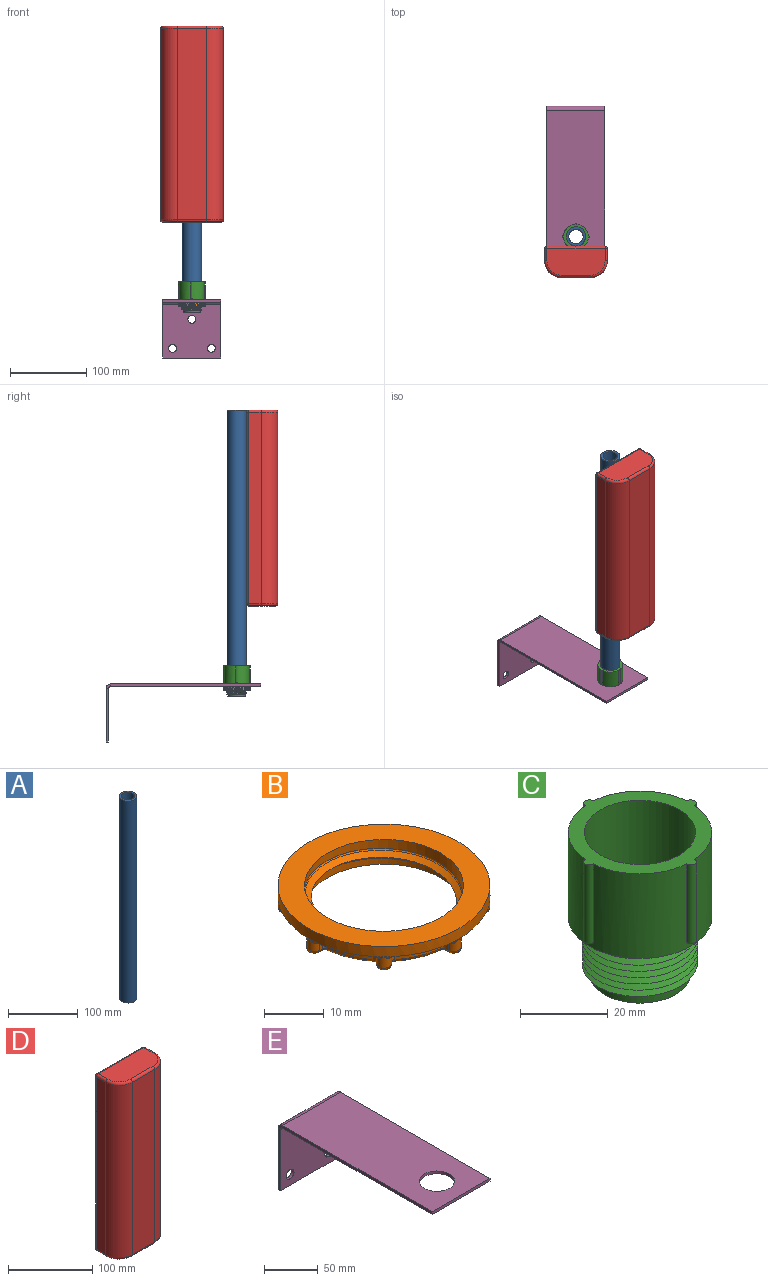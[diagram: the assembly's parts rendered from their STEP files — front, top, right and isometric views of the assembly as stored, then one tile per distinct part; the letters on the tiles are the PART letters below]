
ASSEMBLY  parts=5 mates=4
PART A: 4 faces, bbox 25.4x25.4x355.6 mm
  f0: cylinder r=9.53mm len=355.6mm, axis (0,0,-1), area 21281.7mm2, adj f2,f3
  f1: cylinder r=12.7mm len=355.6mm, axis (0,0,-1), area 28375.6mm2, adj f2,f3
  f2: plane 25.4x25.4mm, normal (0,0,1), area 221.7mm2, adj f0,f1
  f3: plane 25.4x25.4mm, normal (0,0,-1), area 221.7mm2, adj f0,f1
PART B: 196 faces, bbox 36.3x36.3x5.1 mm
  f0: cylinder r=13.33mm len=26.67mm, axis (0,0,1), area 256.3mm2, adj f17,f19,f184,f185,f188,f189,f192,f193
  f1: cylinder r=15.39mm len=7.68mm, axis (0,0,1), area 14.3mm2, adj f20,f57,f75,f157
  f2: plane 10.02x5.12mm, normal (0,0,-1), area 16.9mm2, adj f15,f136,f137,f139,f141,f142
  f3: cylinder r=15.39mm len=7.68mm, axis (0,0,1), area 14.3mm2, adj f52,f55,f87,f139
  f4: plane 10.02x5.12mm, normal (0,0,-1), area 16.9mm2, adj f15,f118,f119,f121,f123,f124
  f5: cylinder r=15.39mm len=7.68mm, axis (0,0,1), area 14.3mm2, adj f47,f50,f99,f121
  f6: plane 10.02x5.12mm, normal (0,0,-1), area 16.9mm2, adj f15,f62,f63,f64,f65,f68
  f7: cylinder r=15.39mm len=7.68mm, axis (0,0,1), area 14.3mm2, adj f42,f45,f68,f111
  f8: plane 10.02x5.12mm, normal (0,0,-1), area 16.9mm2, adj f15,f127,f128,f130,f132,f134
  f9: cylinder r=15.39mm len=7.68mm, axis (0,0,1), area 14.3mm2, adj f37,f40,f110,f130
  f10: plane 10.02x5.12mm, normal (0,0,-1), area 16.9mm2, adj f15,f145,f146,f148,f150,f152
  f11: cylinder r=15.39mm len=7.68mm, axis (0,0,1), area 14.3mm2, adj f32,f35,f98,f148
  f12: plane 10.02x5.12mm, normal (0,0,-1), area 16.9mm2, adj f15,f163,f164,f166,f168,f170
  f13: plane 10.02x5.12mm, normal (0,0,-1), area 16.9mm2, adj f15,f172,f173,f175,f177,f178
  f14: cylinder r=15.39mm len=7.68mm, axis (0,0,1), area 14.3mm2, adj f27,f30,f86,f166
  f15: cylinder r=17.78mm len=35.56mm, axis (0,0,1), area 235.5mm2, adj f2,f4,f6,f8,f10,f12,f13,f16
  f16: plane 10.02x5.12mm, normal (0,0,-1), area 16.9mm2, adj f15,f154,f155,f157,f159,f160
  f17: plane 35.56x35.56mm, normal (0,0,1), area 434.5mm2, adj f0,f15
  f18: cylinder r=15.39mm len=7.68mm, axis (0,0,1), area 14.3mm2, adj f22,f25,f74,f175
  f19: plane 34.29x34.29mm, normal (0,0,-1), area 152.9mm2, adj f0,f69,f70,f71,f72,f73,f74,f75
  f20: cylinder r=0.64mm len=1.7mm, axis (0,0,-1), area 1.6mm2, adj f1,f21,f73,f156
  f21: plane 1.7x0.6mm, normal (-1,0,0), area 1mm2, adj f20,f23,f71,f155
  f22: cylinder r=0.64mm len=1.7mm, axis (0,0,-1), area 1.6mm2, adj f18,f24,f72,f176
  f23: cylinder r=1.27mm len=2.54mm, axis (0,0,-1), area 7.5mm2, adj f21,f24,f69,f153,f154,f178,f179
  f24: plane 1.7x0.6mm, normal (1,0,0), area 1mm2, adj f22,f23,f70,f177
  f25: cylinder r=0.64mm len=1.7mm, axis (0,0,-1), area 1.6mm2, adj f18,f26,f76,f174
  f26: plane 1.7x0.42mm, normal (-0.71,0.71,0), area 1mm2, adj f25,f28,f78,f173
  f27: cylinder r=0.64mm len=1.7mm, axis (0,0,-1), area 1.6mm2, adj f14,f29,f84,f165
  f28: cylinder r=1.27mm len=2.34mm, axis (0,0,-1), area 7.5mm2, adj f26,f29,f80,f162,f163,f171,f172
  f29: plane 1.7x0.42mm, normal (0.71,-0.71,0), area 1mm2, adj f27,f28,f82,f164
  f30: cylinder r=0.64mm len=1.7mm, axis (0,0,-1), area 1.6mm2, adj f14,f31,f88,f167
  f31: plane 1.7x0.6mm, normal (0,1,0), area 1mm2, adj f30,f33,f90,f168
  f32: cylinder r=0.64mm len=1.7mm, axis (0,0,-1), area 1.6mm2, adj f11,f34,f96,f147
  f33: cylinder r=1.27mm len=2.54mm, axis (0,0,-1), area 7.5mm2, adj f31,f34,f92,f144,f145,f169,f170
  f34: plane 1.7x0.6mm, normal (0,-1,0), area 1mm2, adj f32,f33,f94,f146
  f35: cylinder r=0.64mm len=1.7mm, axis (0,0,-1), area 1.6mm2, adj f11,f36,f100,f149
  f36: plane 1.7x0.42mm, normal (0.71,0.71,0), area 1mm2, adj f35,f38,f102,f150
  f37: cylinder r=0.64mm len=1.7mm, axis (0,0,-1), area 1.6mm2, adj f9,f39,f108,f129
  f38: cylinder r=1.27mm len=2.34mm, axis (0,0,-1), area 7.5mm2, adj f36,f39,f104,f126,f127,f151,f152
  f39: plane 1.7x0.42mm, normal (-0.71,-0.71,0), area 1mm2, adj f37,f38,f106,f128
  f40: cylinder r=0.64mm len=1.7mm, axis (0,0,-1), area 1.6mm2, adj f9,f41,f112,f131
  f41: plane 1.7x0.6mm, normal (1,0,0), area 1mm2, adj f40,f43,f114,f132
  f42: cylinder r=0.64mm len=1.7mm, axis (0,0,-1), area 1.6mm2, adj f7,f44,f66,f113
  f43: cylinder r=1.27mm len=2.54mm, axis (0,0,-1), area 7.5mm2, adj f41,f44,f60,f62,f116,f133,f134
  f44: plane 1.7x0.6mm, normal (-1,0,0), area 1mm2, adj f42,f43,f64,f115
  f45: cylinder r=0.64mm len=1.7mm, axis (0,0,-1), area 1.6mm2, adj f7,f46,f67,f109
  f46: plane 1.7x0.42mm, normal (0.71,-0.71,0), area 1mm2, adj f45,f48,f65,f107
  f47: cylinder r=0.64mm len=1.7mm, axis (0,0,-1), area 1.6mm2, adj f5,f49,f101,f122
  f48: cylinder r=1.27mm len=2.34mm, axis (0,0,-1), area 7.5mm2, adj f46,f49,f61,f63,f105,f124,f125
  f49: plane 1.7x0.42mm, normal (-0.71,0.71,0), area 1mm2, adj f47,f48,f103,f123
  f50: cylinder r=0.64mm len=1.7mm, axis (0,0,-1), area 1.6mm2, adj f5,f51,f97,f120
  f51: plane 1.7x0.6mm, normal (0,-1,0), area 1mm2, adj f50,f53,f95,f119
  f52: cylinder r=0.64mm len=1.7mm, axis (0,0,-1), area 1.6mm2, adj f3,f54,f89,f140
  f53: cylinder r=1.27mm len=2.54mm, axis (0,0,-1), area 7.5mm2, adj f51,f54,f93,f117,f118,f142,f143
  f54: plane 1.7x0.6mm, normal (0,1,0), area 1mm2, adj f52,f53,f91,f141
  f55: cylinder r=0.64mm len=1.7mm, axis (0,0,-1), area 1.6mm2, adj f3,f56,f85,f138
  f56: plane 1.7x0.42mm, normal (-0.71,-0.71,0), area 1mm2, adj f55,f58,f83,f137
  f57: cylinder r=0.64mm len=1.7mm, axis (0,0,-1), area 1.6mm2, adj f1,f59,f77,f158
  f58: cylinder r=1.27mm len=2.34mm, axis (0,0,-1), area 7.5mm2, adj f56,f59,f81,f135,f136,f160,f161
  f59: plane 1.7x0.42mm, normal (0.71,0.71,0), area 1mm2, adj f57,f58,f79,f159
  f60: bspline ~1.51x0.66mm, area 0.4mm2, adj f15,f43,f62
  f61: bspline ~1.12x1.02mm, area 0.4mm2, adj f15,f48,f63
  f62: torus R=1.91mm, axis (0,0,1), area 1mm2, adj f6,f43,f60,f64
  f63: torus R=1.91mm, axis (0,0,1), area 1mm2, adj f6,f48,f61,f65
  f64: cylinder r=0.64mm len=0.64mm, axis (0,1,0), area 0.6mm2, adj f6,f44,f62,f66
  f65: cylinder r=0.64mm len=0.87mm, axis (-0.71,-0.71,0), area 0.6mm2, adj f6,f46,f63,f67
  f66: sphere r=0.64mm, area 0.4mm2, adj f42,f64,f68
  f67: sphere r=0.64mm, area 0.7mm2, adj f45,f65,f68
  f68: torus R=16.03mm, axis (0,0,1), area 8.5mm2, adj f6,f7,f66,f67
  f69: torus R=0.64mm, axis (0,0,-1), area 3.3mm2, adj f19,f23,f70,f71
  f70: cylinder r=0.64mm len=0.64mm, axis (0,-1,0), area 0.6mm2, adj f19,f24,f69,f72
  f71: cylinder r=0.64mm len=0.64mm, axis (0,1,0), area 0.6mm2, adj f19,f21,f69,f73
  f72: torus R=1.27mm, axis (0,0,-1), area 1.3mm2, adj f19,f22,f70,f74
  f73: torus R=1.27mm, axis (0,0,-1), area 1.3mm2, adj f19,f20,f71,f75
  f74: torus R=14.76mm, axis (0,0,-1), area 8.3mm2, adj f18,f19,f72,f76
  f75: torus R=14.76mm, axis (0,0,-1), area 8.3mm2, adj f1,f19,f73,f77
  f76: torus R=1.27mm, axis (0,0,-1), area 1.3mm2, adj f19,f25,f74,f78
  f77: torus R=1.27mm, axis (0,0,-1), area 1.3mm2, adj f19,f57,f75,f79
  f78: cylinder r=0.64mm len=0.87mm, axis (0.71,0.71,0), area 0.6mm2, adj f19,f26,f76,f80
  f79: cylinder r=0.64mm len=0.87mm, axis (0.71,-0.71,0), area 0.6mm2, adj f19,f59,f77,f81
  f80: torus R=0.64mm, axis (0,0,-1), area 3.3mm2, adj f19,f28,f78,f82
  f81: torus R=0.64mm, axis (0,0,-1), area 3.3mm2, adj f19,f58,f79,f83
  f82: cylinder r=0.64mm len=0.87mm, axis (-0.71,-0.71,0), area 0.6mm2, adj f19,f29,f80,f84
  f83: cylinder r=0.64mm len=0.87mm, axis (-0.71,0.71,0), area 0.6mm2, adj f19,f56,f81,f85
  f84: torus R=1.27mm, axis (0,0,-1), area 1.3mm2, adj f19,f27,f82,f86
  f85: torus R=1.27mm, axis (0,0,-1), area 1.3mm2, adj f19,f55,f83,f87
  f86: torus R=14.76mm, axis (0,0,-1), area 8.3mm2, adj f14,f19,f84,f88
  f87: torus R=14.76mm, axis (0,0,-1), area 8.3mm2, adj f3,f19,f85,f89
  f88: torus R=1.27mm, axis (0,0,-1), area 1.3mm2, adj f19,f30,f86,f90
  f89: torus R=1.27mm, axis (0,0,-1), area 1.3mm2, adj f19,f52,f87,f91
  f90: cylinder r=0.64mm len=0.64mm, axis (1,0,0), area 0.6mm2, adj f19,f31,f88,f92
  f91: cylinder r=0.64mm len=0.64mm, axis (1,0,0), area 0.6mm2, adj f19,f54,f89,f93
  f92: torus R=0.64mm, axis (0,0,-1), area 3.3mm2, adj f19,f33,f90,f94
  f93: torus R=0.64mm, axis (0,0,-1), area 3.3mm2, adj f19,f53,f91,f95
  f94: cylinder r=0.64mm len=0.64mm, axis (-1,0,0), area 0.6mm2, adj f19,f34,f92,f96
  f95: cylinder r=0.64mm len=0.64mm, axis (-1,0,0), area 0.6mm2, adj f19,f51,f93,f97
  f96: torus R=1.27mm, axis (0,0,-1), area 1.3mm2, adj f19,f32,f94,f98
  f97: torus R=1.27mm, axis (0,0,-1), area 1.3mm2, adj f19,f50,f95,f99
  f98: torus R=14.76mm, axis (0,0,-1), area 8.3mm2, adj f11,f19,f96,f100
  f99: torus R=14.76mm, axis (0,0,-1), area 8.3mm2, adj f5,f19,f97,f101
  f100: torus R=1.27mm, axis (0,0,-1), area 1.3mm2, adj f19,f35,f98,f102
  f101: torus R=1.27mm, axis (0,0,-1), area 1.3mm2, adj f19,f47,f99,f103
  f102: cylinder r=0.64mm len=0.87mm, axis (0.71,-0.71,0), area 0.6mm2, adj f19,f36,f100,f104
  f103: cylinder r=0.64mm len=0.87mm, axis (0.71,0.71,0), area 0.6mm2, adj f19,f49,f101,f105
  f104: torus R=0.64mm, axis (0,0,-1), area 3.3mm2, adj f19,f38,f102,f106
  f105: torus R=0.64mm, axis (0,0,-1), area 3.3mm2, adj f19,f48,f103,f107
  f106: cylinder r=0.64mm len=0.87mm, axis (-0.71,0.71,0), area 0.6mm2, adj f19,f39,f104,f108
  f107: cylinder r=0.64mm len=0.87mm, axis (-0.71,-0.71,0), area 0.6mm2, adj f19,f46,f105,f109
  f108: torus R=1.27mm, axis (0,0,-1), area 1.3mm2, adj f19,f37,f106,f110
  f109: torus R=1.27mm, axis (0,0,-1), area 1.3mm2, adj f19,f45,f107,f111
  f110: torus R=14.76mm, axis (0,0,-1), area 8.3mm2, adj f9,f19,f108,f112
  f111: torus R=14.76mm, axis (0,0,-1), area 8.3mm2, adj f7,f19,f109,f113
  f112: torus R=1.27mm, axis (0,0,-1), area 1.3mm2, adj f19,f40,f110,f114
  f113: torus R=1.27mm, axis (0,0,-1), area 1.3mm2, adj f19,f42,f111,f115
  f114: cylinder r=0.64mm len=0.64mm, axis (0,-1,0), area 0.6mm2, adj f19,f41,f112,f116
  f115: cylinder r=0.64mm len=0.64mm, axis (0,1,0), area 0.6mm2, adj f19,f44,f113,f116
  f116: torus R=0.64mm, axis (0,0,-1), area 3.3mm2, adj f19,f43,f114,f115
  f117: bspline ~1.51x0.66mm, area 0.6mm2, adj f15,f53,f118
  f118: torus R=1.91mm, axis (0,0,1), area 1mm2, adj f4,f53,f117,f119
  f119: cylinder r=0.64mm len=0.64mm, axis (-1,0,0), area 0.6mm2, adj f4,f51,f118,f120
  f120: sphere r=0.64mm, area 0.4mm2, adj f50,f119,f121
  f121: torus R=16.03mm, axis (0,0,1), area 8.5mm2, adj f4,f5,f120,f122
  f122: sphere r=0.64mm, area 0.6mm2, adj f47,f121,f123
  f123: cylinder r=0.64mm len=0.87mm, axis (0.71,0.71,0), area 0.6mm2, adj f4,f49,f122,f124
  f124: torus R=1.91mm, axis (0,0,1), area 1mm2, adj f4,f48,f123,f125
  f125: bspline ~1.12x1.02mm, area 0.4mm2, adj f15,f48,f124
  f126: bspline ~1.12x1.02mm, area 0.4mm2, adj f15,f38,f127
  f127: torus R=1.91mm, axis (0,0,1), area 1mm2, adj f8,f38,f126,f128
  f128: cylinder r=0.64mm len=0.87mm, axis (-0.71,0.71,0), area 0.6mm2, adj f8,f39,f127,f129
  f129: sphere r=0.64mm, area 0.7mm2, adj f37,f128,f130
  f130: torus R=16.03mm, axis (0,0,1), area 8.5mm2, adj f8,f9,f129,f131
  f131: sphere r=0.64mm, area 0.8mm2, adj f40,f130,f132
  f132: cylinder r=0.64mm len=0.64mm, axis (0,-1,0), area 0.6mm2, adj f8,f41,f131,f134
  f133: bspline ~1.51x0.66mm, area 0.4mm2, adj f15,f43,f134
  f134: torus R=1.91mm, axis (0,0,1), area 1mm2, adj f8,f43,f132,f133
  f135: bspline ~1.12x1.02mm, area 0.4mm2, adj f15,f58,f136
  f136: torus R=1.91mm, axis (0,0,1), area 1mm2, adj f2,f58,f135,f137
  f137: cylinder r=0.64mm len=0.87mm, axis (-0.71,0.71,0), area 0.6mm2, adj f2,f56,f136,f138
  f138: sphere r=0.64mm, area 0.6mm2, adj f55,f137,f139
  f139: torus R=16.03mm, axis (0,0,1), area 8.5mm2, adj f2,f3,f138,f140
  f140: sphere r=0.64mm, area 0.6mm2, adj f52,f139,f141
  f141: cylinder r=0.64mm len=0.64mm, axis (1,0,0), area 0.6mm2, adj f2,f54,f140,f142
  f142: torus R=1.91mm, axis (0,0,1), area 1mm2, adj f2,f53,f141,f143
  f143: bspline ~1.51x0.66mm, area 0.4mm2, adj f15,f53,f142
  f144: bspline ~1.51x0.66mm, area 0.4mm2, adj f15,f33,f145
  f145: torus R=1.91mm, axis (0,0,1), area 1mm2, adj f10,f33,f144,f146
  f146: cylinder r=0.64mm len=0.64mm, axis (-1,0,0), area 0.6mm2, adj f10,f34,f145,f147
  f147: sphere r=0.64mm, area 0.6mm2, adj f32,f146,f148
  f148: torus R=16.03mm, axis (0,0,1), area 8.5mm2, adj f10,f11,f147,f149
  f149: sphere r=0.64mm, area 0.7mm2, adj f35,f148,f150
  f150: cylinder r=0.64mm len=0.87mm, axis (0.71,-0.71,0), area 0.6mm2, adj f10,f36,f149,f152
  f151: bspline ~1.12x1.02mm, area 0.4mm2, adj f15,f38,f152
  f152: torus R=1.91mm, axis (0,0,1), area 1mm2, adj f10,f38,f150,f151
  f153: bspline ~1.51x0.66mm, area 0.6mm2, adj f15,f23,f154
  f154: torus R=1.91mm, axis (0,0,1), area 1mm2, adj f16,f23,f153,f155
  f155: cylinder r=0.64mm len=0.64mm, axis (0,1,0), area 0.6mm2, adj f16,f21,f154,f156
  f156: sphere r=0.64mm, area 0.6mm2, adj f20,f155,f157
  f157: torus R=16.03mm, axis (0,0,1), area 8.5mm2, adj f1,f16,f156,f158
  f158: sphere r=0.64mm, area 0.6mm2, adj f57,f157,f159
  f159: cylinder r=0.64mm len=0.87mm, axis (0.71,-0.71,0), area 0.6mm2, adj f16,f59,f158,f160
  f160: torus R=1.91mm, axis (0,0,1), area 1mm2, adj f16,f58,f159,f161
  f161: bspline ~1.12x1.02mm, area 0.4mm2, adj f15,f58,f160
  f162: bspline ~1.12x1.02mm, area 0.4mm2, adj f15,f28,f163
  f163: torus R=1.91mm, axis (0,0,1), area 1mm2, adj f12,f28,f162,f164
  f164: cylinder r=0.64mm len=0.87mm, axis (-0.71,-0.71,0), area 0.6mm2, adj f12,f29,f163,f165
  f165: sphere r=0.64mm, area 0.8mm2, adj f27,f164,f166
  f166: torus R=16.03mm, axis (0,0,1), area 8.5mm2, adj f12,f14,f165,f167
  f167: sphere r=0.64mm, area 0.8mm2, adj f30,f166,f168
  f168: cylinder r=0.64mm len=0.64mm, axis (1,0,0), area 0.6mm2, adj f12,f31,f167,f170
  f169: bspline ~1.51x0.66mm, area 0.6mm2, adj f15,f33,f170
  f170: torus R=1.91mm, axis (0,0,1), area 1mm2, adj f12,f33,f168,f169
  f171: bspline ~1.12x1.02mm, area 0.4mm2, adj f15,f28,f172
  f172: torus R=1.91mm, axis (0,0,1), area 1mm2, adj f13,f28,f171,f173
  f173: cylinder r=0.64mm len=0.87mm, axis (0.71,0.71,0), area 0.6mm2, adj f13,f26,f172,f174
  f174: sphere r=0.64mm, area 0.6mm2, adj f25,f173,f175
  f175: torus R=16.03mm, axis (0,0,1), area 8.5mm2, adj f13,f18,f174,f176
  f176: sphere r=0.64mm, area 0.6mm2, adj f22,f175,f177
  f177: cylinder r=0.64mm len=0.64mm, axis (0,-1,0), area 0.6mm2, adj f13,f24,f176,f178
  f178: torus R=1.91mm, axis (0,0,1), area 1mm2, adj f13,f23,f177,f179
  f179: bspline ~1.51x0.66mm, area 0.5mm2, adj f15,f23,f178
  f180: bspline ~30.8x26.67mm, area 94mm2, adj f181,f184,f186,f187,f191
  f181: bspline ~30.8x26.67mm, area 93.9mm2, adj f180,f186,f190,f191,f195
  f182: plane 0.29x0.2mm, normal (-1,0,0), area 0mm2, adj f186,f189,f190
  f183: plane 0.29x0.2mm, normal (1,0,0), area 0mm2, adj f187,f191,f192
  f184: bspline ~26.68x26.62mm, area 28.6mm2, adj f0,f180,f185,f188
  f185: bspline ~1.15x0.87mm, area 0.4mm2, adj f0,f184,f186,f189
  f186: bspline ~1.64x1.35mm, area 0.5mm2, adj f180,f181,f182,f185,f190
  f187: bspline ~1.57x1.28mm, area 0.4mm2, adj f180,f183,f188,f191
  f188: bspline ~0.99x0.85mm, area 0.4mm2, adj f0,f184,f187,f192
  f189: cylinder r=0.38mm len=0.38mm, axis (0,0,1), area 0.2mm2, adj f0,f182,f185,f193
  f190: bspline ~1.57x1.29mm, area 0.4mm2, adj f181,f182,f186,f193
  f191: bspline ~1.65x1.35mm, area 0.5mm2, adj f180,f181,f183,f187,f194
  f192: cylinder r=0.38mm len=0.38mm, axis (0,0,1), area 0.2mm2, adj f0,f183,f188,f194
  f193: bspline ~0.99x0.85mm, area 0.4mm2, adj f0,f189,f190,f195
  f194: bspline ~1.15x0.87mm, area 0.4mm2, adj f0,f191,f192,f195
  f195: bspline ~26.68x26.62mm, area 28.6mm2, adj f0,f181,f193,f194
PART C: 29 faces, bbox 36.5x36.5x40.7 mm
  f0: cylinder r=11.56mm len=23.11mm, axis (0,0,1), area 129.3mm2, adj f1,f23,f24,f25,f27
  f1: cylinder r=11.56mm len=23.11mm, axis (0,0,1), area 4.3mm2, adj f0,f2,f27,f28
  f2: cylinder r=11.56mm len=23.11mm, axis (0,0,1), area 4.2mm2, adj f1,f3,f27,f28
  f3: cylinder r=11.56mm len=23.11mm, axis (0,0,1), area 4.3mm2, adj f2,f4,f27,f28
  f4: cylinder r=11.56mm len=23.11mm, axis (0,0,1), area 4.3mm2, adj f3,f5,f27,f28
  f5: cylinder r=11.56mm len=23.11mm, axis (0,0,1), area 4.3mm2, adj f4,f6,f27,f28
  f6: cylinder r=11.56mm len=23.11mm, axis (0,0,1), area 4.3mm2, adj f5,f7,f27,f28
  f7: cylinder r=11.56mm len=23.11mm, axis (0,0,1), area 4.3mm2, adj f6,f8,f27,f28
  f8: cylinder r=11.56mm len=23.11mm, axis (0,0,1), area 11.3mm2, adj f7,f10,f26,f28
  f9: cylinder r=16.38mm len=32.77mm, axis (0,0,1), area 2208.3mm2, adj f10,f12,f14,f15,f16,f17,f18,f19
  f10: plane 34x34mm, normal (0,0,-1), area 382.5mm2, adj f8,f9,f26,f28
  f11: cylinder r=12.7mm len=25.4mm, axis (0,0,-1), area 1591.1mm2, adj f12,f13
  f12: plane 35.31x35.31mm, normal (0,0,1), area 346.8mm2, adj f9,f11,f14,f16,f18,f20
  f13: plane 25.4x25.4mm, normal (0,0,1), area 221.7mm2, adj f11,f22
  f14: cylinder r=1.27mm len=21.97mm, axis (0,0,-1), area 89.8mm2, adj f9,f12,f15
  f15: plane 2.54x1.32mm, normal (0,0,-1), area 2.6mm2, adj f9,f14
  f16: cylinder r=1.27mm len=21.97mm, axis (0,0,-1), area 89.8mm2, adj f9,f12,f17
  f17: plane 2.54x1.32mm, normal (0,0,-1), area 2.6mm2, adj f9,f16
  f18: cylinder r=1.27mm len=21.97mm, axis (0,0,-1), area 89.8mm2, adj f9,f12,f19
  f19: plane 2.54x1.32mm, normal (0,0,-1), area 2.6mm2, adj f9,f18
  f20: cylinder r=1.27mm len=21.97mm, axis (0,0,-1), area 89.8mm2, adj f9,f12,f21
  f21: plane 2.54x1.32mm, normal (0,0,-1), area 2.6mm2, adj f9,f20
  f22: cylinder r=9.53mm len=19.56mm, axis (0,0,1), area 1170.5mm2, adj f13,f23
  f23: plane 23.11x23.11mm, normal (0,0,-1), area 134.6mm2, adj f0,f22
  f24: bspline ~12.49x11.51mm, area 15.8mm2, adj f0,f25,f27
  f25: bspline ~12.49x11.51mm, area 15.8mm2, adj f0,f24,f28
  f26: bspline ~12.49x11.51mm, area 15.8mm2, adj f8,f10,f27
  f27: bspline ~30.44x26.37mm, area 1142.9mm2, adj f0,f1,f2,f3,f4,f5,f6,f7
  f28: bspline ~30.44x26.37mm, area 1105.5mm2, adj f1,f2,f3,f4,f5,f6,f7,f8
PART D: 26 faces, bbox 86.2x43.1x257.2 mm
  f0: plane 250.83x15.88mm, normal (1,0,0), area 3981.8mm2, adj f7,f10,f15,f20
  f1: plane 76.2x34.93mm, normal (0,0,1), area 2505.5mm2, adj f19,f20,f22,f23,f24,f25
  f2: plane 250.83x15.88mm, normal (-1,0,0), area 3981.8mm2, adj f6,f13,f18,f23
  f3: plane 76.2x34.93mm, normal (0,0,-1), area 2505.5mm2, adj f8,f9,f10,f11,f13,f14
  f4: plane 250.83x38.1mm, normal (0,-1,0), area 9556.4mm2, adj f6,f7,f9,f24
  f5: plane 250.83x76.2mm, normal (0,1,0), area 19112.9mm2, adj f14,f15,f18,f19
  f6: cylinder r=22.23mm len=250.83mm, axis (0,0,1), area 8756.5mm2, adj f2,f4,f11,f25
  f7: cylinder r=22.23mm len=250.83mm, axis (0,0,-1), area 8756.5mm2, adj f0,f4,f8,f22
  f8: torus R=19.05mm, axis (0,0,-1), area 165.1mm2, adj f3,f7,f9,f10
  f9: cylinder r=3.17mm len=38.1mm, axis (-1,0,0), area 190mm2, adj f3,f4,f8,f11
  f10: cylinder r=3.17mm len=15.88mm, axis (0,1,0), area 79.2mm2, adj f0,f3,f8,f12
  f11: torus R=19.05mm, axis (0,0,-1), area 165.1mm2, adj f3,f6,f9,f13
  f12: sphere r=3.17mm, area 15.8mm2, adj f10,f14,f15
  f13: cylinder r=3.17mm len=15.88mm, axis (0,-1,0), area 79.2mm2, adj f2,f3,f11,f16
  f14: cylinder r=3.17mm len=76.2mm, axis (1,0,0), area 380mm2, adj f3,f5,f12,f16
  f15: cylinder r=3.17mm len=250.83mm, axis (0,0,1), area 1250.9mm2, adj f0,f5,f12,f17
  f16: sphere r=3.17mm, area 15.8mm2, adj f13,f14,f18
  f17: sphere r=3.17mm, area 15.8mm2, adj f15,f19,f20
  f18: cylinder r=3.17mm len=250.83mm, axis (0,0,-1), area 1250.9mm2, adj f2,f5,f16,f21
  f19: cylinder r=3.17mm len=76.2mm, axis (-1,0,0), area 380mm2, adj f1,f5,f17,f21
  f20: cylinder r=3.17mm len=15.88mm, axis (0,-1,0), area 79.2mm2, adj f0,f1,f17,f22
  f21: sphere r=3.17mm, area 15.8mm2, adj f18,f19,f23
  f22: torus R=19.05mm, axis (0,0,-1), area 165.1mm2, adj f1,f7,f20,f24
  f23: cylinder r=3.17mm len=15.88mm, axis (0,1,0), area 79.2mm2, adj f1,f2,f21,f25
  f24: cylinder r=3.17mm len=38.1mm, axis (1,0,0), area 190mm2, adj f1,f4,f22,f25
  f25: torus R=19.05mm, axis (0,0,-1), area 165.1mm2, adj f1,f6,f23,f24
PART E: 18 faces, bbox 76.2x203.2x76.2 mm
  f0: plane 196.85x3.18mm, normal (1,0,0), area 625mm2, adj f2,f4,f5,f14
  f1: plane 196.85x3.18mm, normal (-1,0,0), area 625mm2, adj f2,f4,f5,f15
  f2: plane 76.2x3.18mm, normal (0,-1,0), area 241.9mm2, adj f0,f1,f4,f5
  f3: cylinder r=16.38mm len=32.77mm, axis (0,0,-1), area 326.8mm2, adj f4,f5
  f4: plane 196.85x76.2mm, normal (0,0,1), area 14156.8mm2, adj f0,f1,f2,f3,f16
  f5: plane 196.85x76.2mm, normal (0,0,-1), area 14156.8mm2, adj f0,f1,f2,f3,f17
  f6: plane 76.2x3.18mm, normal (0,0,-1), area 241.9mm2, adj f7,f11,f12,f13
  f7: plane 69.85x3.18mm, normal (-1,0,0), area 221.8mm2, adj f6,f12,f13,f15
  f8: cylinder r=5.22mm len=10.44mm, axis (0,1,0), area 104.1mm2, adj f12,f13
  f9: cylinder r=5.22mm len=10.44mm, axis (0,1,0), area 104.1mm2, adj f12,f13
  f10: cylinder r=5.22mm len=10.44mm, axis (0,1,0), area 104.1mm2, adj f12,f13
  f11: plane 69.85x3.18mm, normal (1,0,0), area 221.8mm2, adj f6,f12,f13,f14
  f12: plane 76.2x69.85mm, normal (0,1,0), area 5065.8mm2, adj f6,f7,f8,f9,f10,f11,f16
  f13: plane 76.2x69.85mm, normal (0,-1,0), area 5065.8mm2, adj f6,f7,f8,f9,f10,f11,f17
  f14: plane 6.35x6.35mm, normal (1,0,0), area 23.8mm2, adj f0,f11,f16,f17
  f15: plane 6.35x6.35mm, normal (-1,0,0), area 23.8mm2, adj f1,f7,f16,f17
  f16: cylinder r=6.35mm len=76.2mm, axis (1,0,0), area 760.1mm2, adj f4,f12,f14,f15
  f17: cylinder r=3.17mm len=76.2mm, axis (1,0,0), area 380mm2, adj f5,f13,f14,f15
PLACE A t=(31.31,-54.23,38.11)mm
PLACE B t=(31.31,-54.23,76.21)mm
PLACE C t=(31.31,-54.23,38.11)mm
PLACE D t=(31.41,19.37,38.11)mm
PLACE E t=(31.31,-54.23,38.11)mm fixed
MATE planar A.f1 <-> D.f1  axis (0,0,1) through (31.31,-54.23,393.71)mm
MATE fastened E.f3 <-> B.f0  axis (0,0,-1) through (31.31,-54.23,31.25)mm
MATE fastened A.f1 <-> C.f11  axis (0,0,-1) through (31.31,-54.23,38.11)mm
MATE fastened C.f9 <-> E.f3  axis (0,0,-1) through (31.31,-54.23,34.42)mm
